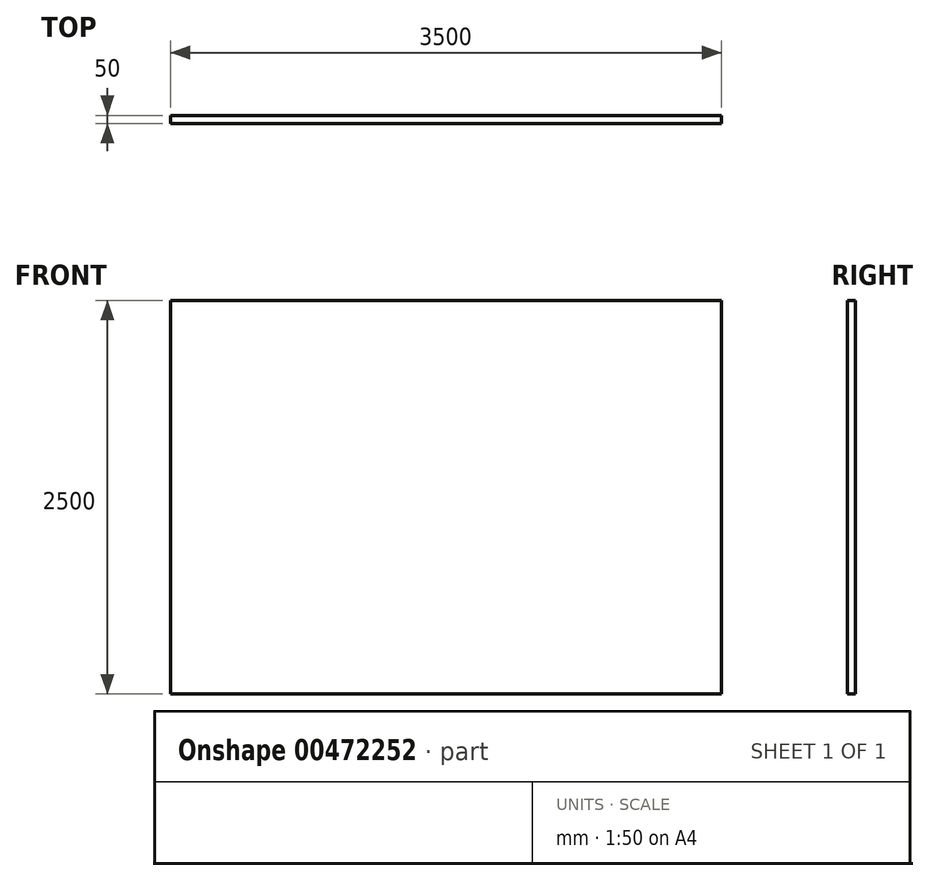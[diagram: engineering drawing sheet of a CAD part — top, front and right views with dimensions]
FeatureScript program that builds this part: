
annotation { "Feature Type Name" : "Feature", "Feature Type Description" : "" }
export const myFeature = defineFeature(function(context is Context, id is Id, definition is map)
    precondition{}
    {
        {
            var Q0;
            Q0=qCreatedBy(makeId("Front.planeOp"),FACE);
            var sketch = newSketch(context, id + "F0", { "sketchPlane" : qUnion([Q0])});
            skLineSegment(sketch, "E0.bottom", {"start": v(0, 0) * mm, "end": v(-3500, 0) * mm});
            skLineSegment(sketch, "E0.top", {"start": v(0, 2500) * mm, "end": v(-3500, 2500) * mm});
            skLineSegment(sketch, "E0.left", {"start": v(0, 0) * mm, "end": v(0, 2500) * mm});
            skLineSegment(sketch, "E0.right", {"start": v(-3500, 0) * mm, "end": v(-3500, 2500) * mm});
            skSolve(sketch);
        }
        {
            var Q0;
            Q0=makeQuery(id+"F0.imprint","IMPRINT",FACE,{"disambiguationData":[TD([[makeQuery(id+"F0.imprint","IMPRINT",EDGE,{"derivedFrom":sQuery(id+"F0.wireOp",EDGE,"E0.bottom")}),-1.0]])]});
            extrude(context, id + "F1", {"entities" : qUnion([Q0]), "depth" : 50 * mm});
        }
    });
